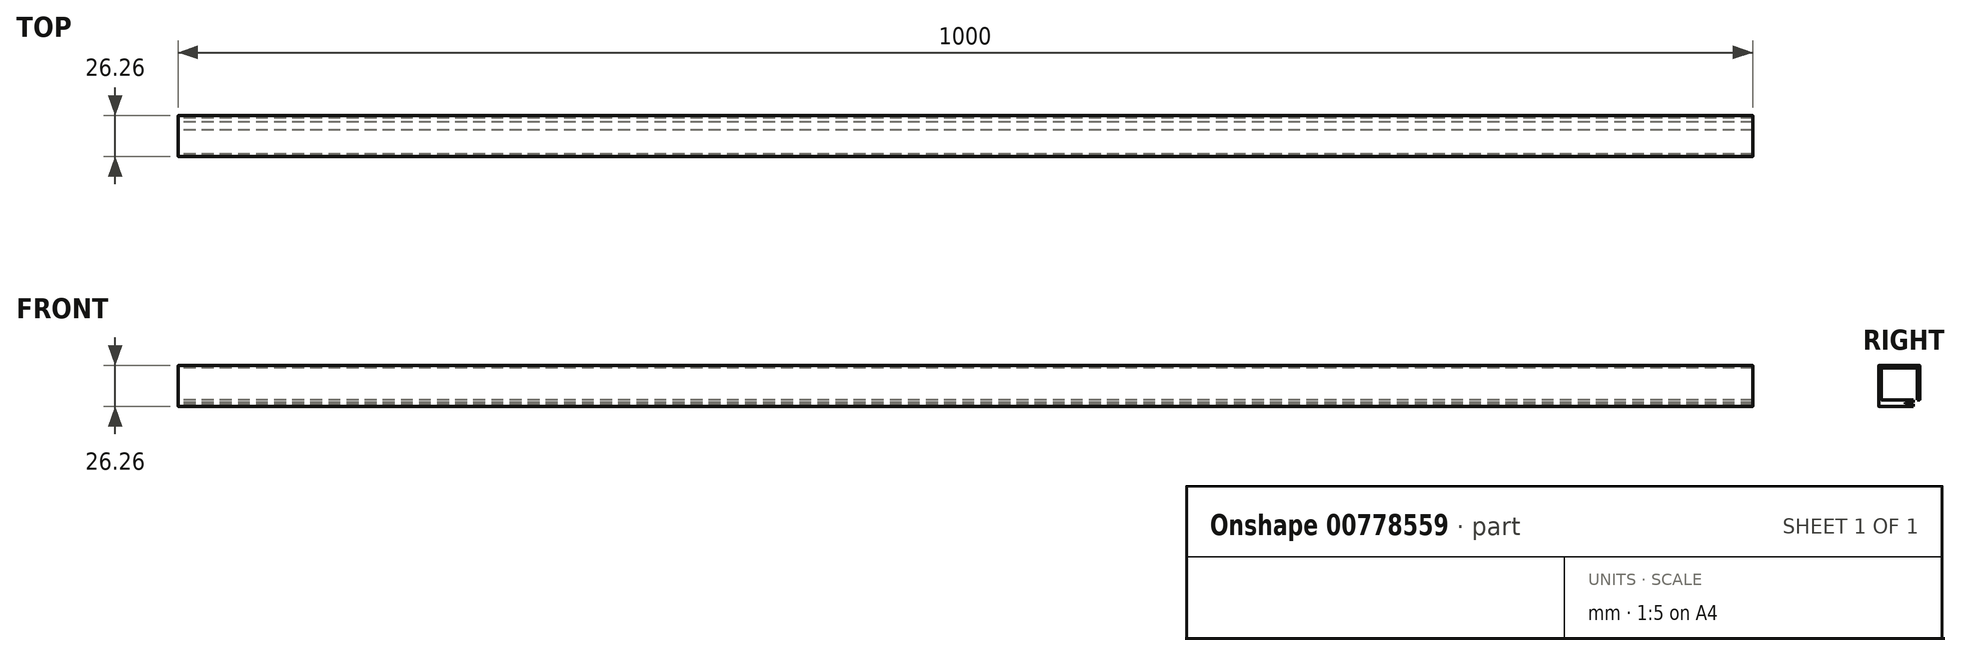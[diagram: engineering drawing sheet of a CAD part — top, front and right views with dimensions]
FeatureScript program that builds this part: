
annotation { "Feature Type Name" : "Feature", "Feature Type Description" : "" }
export const myFeature = defineFeature(function(context is Context, id is Id, definition is map)
    precondition{}
    {
        {
            var Q0;
            Q0=qCreatedBy(makeId("Right.planeOp"),FACE);
            var sketch = newSketch(context, id + "F0", { "sketchPlane" : qUnion([Q0])});
            skLineSegment(sketch, "E0.bottom", {"start": v(25.96, 26.26) * mm, "end": v(0.3, 26.26) * mm});
            skPoint(sketch, "E0.middle", {"position": v(0, 0) * mm});
            skLineSegment(sketch, "E1", {"start": v(1.9, 24.66) * mm, "end": v(24.36, 24.66) * mm});
            skLineSegment(sketch, "E2", {"start": v(26.26, 4.56) * mm, "end": v(26.26, 25.96) * mm});
            skPoint(sketch, "E3.orphan", {"position": v(8.65, 33.22) * mm});
            skPoint(sketch, "E4.start.orphan", {"position": v(0.3, 0) * mm});
            skLineSegment(sketch, "E5.trimOffspring", {"start": v(24.66, 4.26) * mm, "end": v(24.66, 24.36) * mm});
            skPoint(sketch, "E6.visualSharp", {"position": v(31.16, 0) * mm});
            skPoint(sketch, "E7.visualSharp", {"position": v(30.96, 4.68) * mm});
            skPoint(sketch, "E8.visualSharp", {"position": v(9.15, 7.2) * mm});
            skLineSegment(sketch, "E9", {"start": v(0, 0.3) * mm, "end": v(0, 25.96) * mm});
            skLineSegment(sketch, "E10", {"start": v(1.6, 24.36) * mm, "end": v(1.6, 4.5) * mm});
            skPoint(sketch, "E11.end.orphan", {"position": v(7.64, 6.95) * mm});
            skPoint(sketch, "E12.visualSharp", {"position": v(22, -1.17) * mm});
            skPoint(sketch, "E13.visualSharp", {"position": v(6.43, 18.13) * mm});
            skPoint(sketch, "E14.end.orphan", {"position": v(5.93, 7.88) * mm});
            skPoint(sketch, "E15.start.orphan", {"position": v(33.48, 11.89) * mm});
            skPoint(sketch, "E7.filletArc.end.orphan", {"position": v(35.37, 11.06) * mm});
            skPoint(sketch, "E16.end.orphan", {"position": v(21.05, 4.82) * mm});
            skLineSegment(sketch, "E17", {"start": v(25.96, 4.26) * mm, "end": v(24.66, 4.26) * mm});
            skPoint(sketch, "E18.visualSharp", {"position": v(19.88, 7.8) * mm});
            skPoint(sketch, "E19.visualSharp", {"position": v(42.98, 6.39) * mm});
            skPoint(sketch, "E20.visualSharp", {"position": v(19.88, 10.75) * mm});
            skPoint(sketch, "E21.visualSharp", {"position": v(28.07, 11.02) * mm});
            skPoint(sketch, "E22.visualSharp", {"position": v(18.13, 9.47) * mm});
            skPoint(sketch, "E23.visualSharp", {"position": v(24.66, 5.96) * mm});
            skPoint(sketch, "E24.visualSharp", {"position": v(24.66, 4.26) * mm});
            skPoint(sketch, "E25.visualSharp", {"position": v(19.06, 9.02) * mm});
            skPoint(sketch, "E26.visualSharp", {"position": v(26.26, 4.26) * mm});
            skArc(sketch, "E26.filletArc", {"start": v(25.96, 4.26) * mm, "mid": v(26.18, 4.35) * mm, "end": v(26.26, 4.56) * mm});
            skPoint(sketch, "E27.visualSharp", {"position": v(22, 0) * mm});
            skArc(sketch, "E28.filletArc", {"start": v(0, 0.3) * mm, "mid": v(0.09, 0.09) * mm, "end": v(0.3, 0) * mm});
            skPoint(sketch, "E29.visualSharp", {"position": v(1.6, 4.2) * mm});
            skArc(sketch, "E29.filletArc", {"start": v(1.6, 4.5) * mm, "mid": v(1.69, 4.29) * mm, "end": v(1.9, 4.2) * mm});
            skPoint(sketch, "E30.visualSharp", {"position": v(1.6, 24.66) * mm});
            skArc(sketch, "E30.filletArc", {"start": v(1.9, 24.66) * mm, "mid": v(1.69, 24.58) * mm, "end": v(1.6, 24.36) * mm});
            skPoint(sketch, "E31.visualSharp", {"position": v(0, 26.26) * mm});
            skArc(sketch, "E31.filletArc", {"start": v(0.3, 26.26) * mm, "mid": v(0.09, 26.18) * mm, "end": v(0, 25.96) * mm});
            skPoint(sketch, "E32.visualSharp", {"position": v(24.66, 24.66) * mm});
            skArc(sketch, "E32.filletArc", {"start": v(24.66, 24.36) * mm, "mid": v(24.58, 24.58) * mm, "end": v(24.36, 24.66) * mm});
            skPoint(sketch, "E33.visualSharp", {"position": v(26.26, 26.26) * mm});
            skArc(sketch, "E33.filletArc", {"start": v(26.26, 25.96) * mm, "mid": v(26.18, 26.18) * mm, "end": v(25.96, 26.26) * mm});
            skLineSegment(sketch, "E34", {"start": v(26.26, 4.56) * mm, "end": v(26.26, 4.26) * mm, "construction": true});
            skLineSegment(sketch, "E35", {"start": v(21.7, 0) * mm, "end": v(21.7, 0) * mm});
            skPoint(sketch, "E36.start.orphan", {"position": v(21.13, 7.8) * mm});
            skPoint(sketch, "E37.end.orphan", {"position": v(42.98, 13.3) * mm});
            skLineSegment(sketch, "E38.trimOffspring", {"start": v(0.3, 0) * mm, "end": v(0.3, 0) * mm});
            skLineSegment(sketch, "E39", {"start": v(0.3, 0) * mm, "end": v(22, 0) * mm});
            skLineSegment(sketch, "E40", {"start": v(1.9, 4.2) * mm, "end": v(22, 4.2) * mm});
            skLineSegment(sketch, "E41", {"start": v(22, 0) * mm, "end": v(22, 1.58) * mm});
            skLineSegment(sketch, "E42", {"start": v(22, 1.58) * mm, "end": v(22, 1.58) * mm});
            skLineSegment(sketch, "E43", {"start": v(22, 1.58) * mm, "end": v(17, 1.58) * mm});
            skLineSegment(sketch, "E44", {"start": v(17, 1.58) * mm, "end": v(17, 2.63) * mm});
            skLineSegment(sketch, "E45", {"start": v(17, 2.63) * mm, "end": v(22, 2.63) * mm});
            skLineSegment(sketch, "E46", {"start": v(22, 4.2) * mm, "end": v(22, 2.63) * mm});
            skSolve(sketch);
        }
        {
            var Q0;
            Q0=qSketchRegion(id+"F0",true);
            extrude(context, id + "F1", {"entities" : qUnion([Q0]), "depth" : 1000 * mm, "offsetDistance" : 25 * mm});
        }
    });
